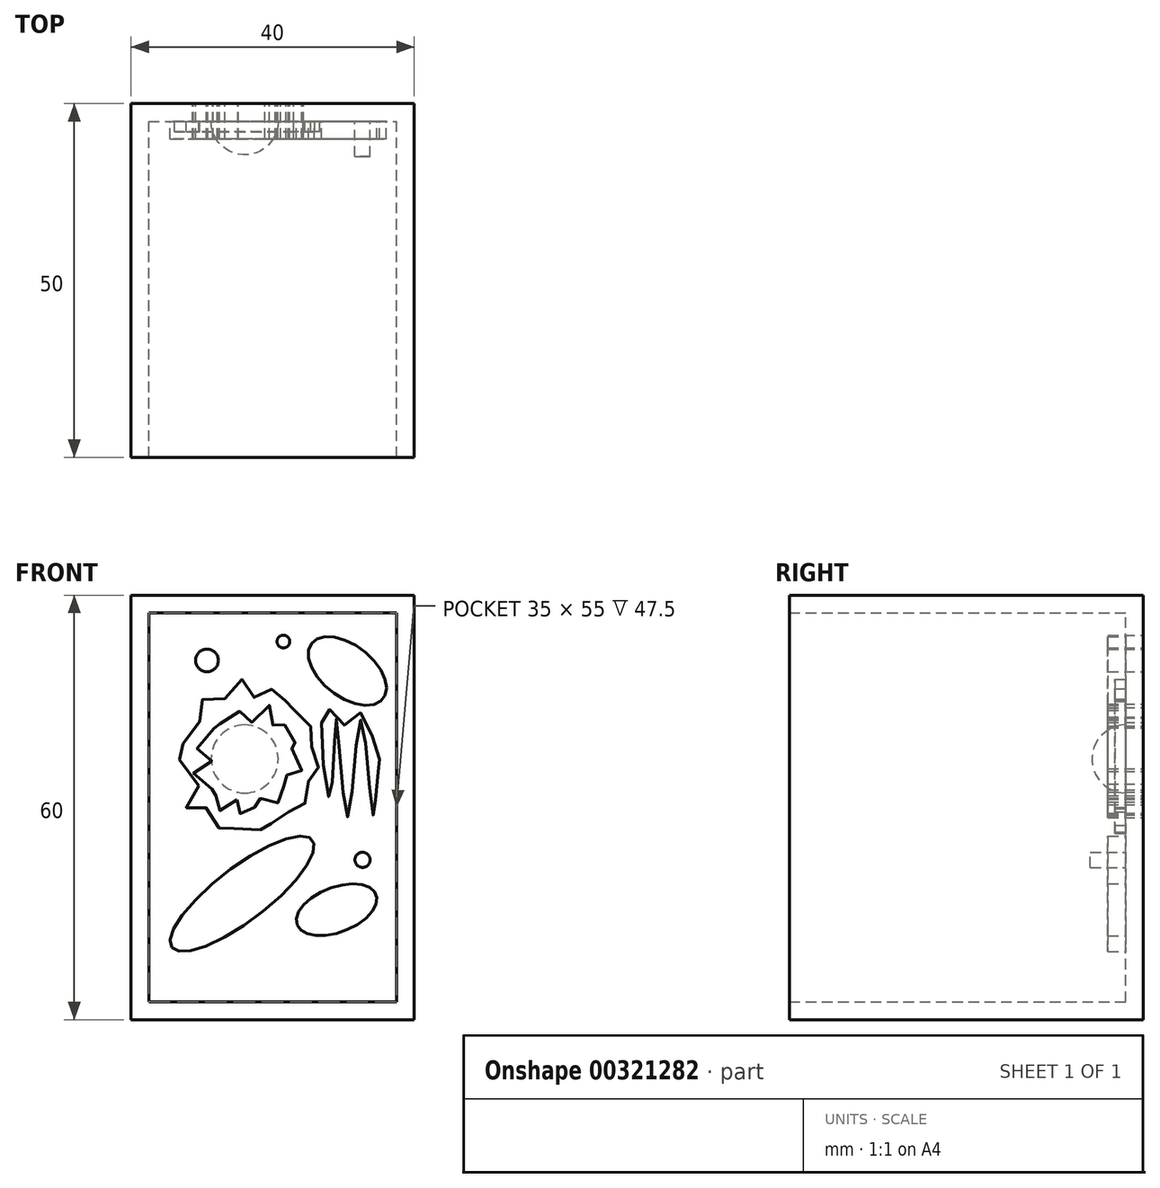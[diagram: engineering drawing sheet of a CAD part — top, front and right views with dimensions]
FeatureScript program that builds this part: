
annotation { "Feature Type Name" : "Feature", "Feature Type Description" : "" }
export const myFeature = defineFeature(function(context is Context, id is Id, definition is map)
    precondition{}
    {
        {
            var Q0;
            Q0=qCreatedBy(makeId("Front.planeOp"),FACE);
            var sketch = newSketch(context, id + "F0", { "sketchPlane" : qUnion([Q0])});
            skLineSegment(sketch, "E0.bottom", {"start": v(0, 0) * mm, "end": v(40, 0) * mm});
            skLineSegment(sketch, "E0.top", {"start": v(0, 60) * mm, "end": v(40, 60) * mm});
            skLineSegment(sketch, "E0.left", {"start": v(0, 0) * mm, "end": v(0, 60) * mm});
            skLineSegment(sketch, "E0.right", {"start": v(40, 0) * mm, "end": v(40, 60) * mm});
            skSolve(sketch);
        }
        {
            var Q0;
            Q0=makeQuery(id+"F0.imprint","IMPRINT",FACE,{"disambiguationData":[TD([[makeQuery(id+"F0.imprint","IMPRINT",EDGE,{"derivedFrom":sQuery(id+"F0.wireOp",EDGE,"E0.bottom")}),1.0]])]});
            extrude(context, id + "F1", {"entities" : qUnion([Q0]), "depth" : 25 * mm});
        }
        {
            var Q0;
            Q0=makeQuery(id+"F1.opExtrude","CAP_FACE",FACE,{"disambiguationData":[OSD([sQuery(id+"F0.wireOp",EDGE,"E0.bottom"),sQuery(id+"F0.wireOp",EDGE,"E0.top"),sQuery(id+"F0.wireOp",EDGE,"E0.left"),sQuery(id+"F0.wireOp",EDGE,"E0.right")])],"isStart":false});
            extrude(context, id + "F2", {"entities" : qUnion([Q0]), "operationType" : NewBodyOperationType.ADD, "depth" : 25 * mm});
        }
        {
            var Q0;
            Q0=makeQuery(id+"F2.opExtrude","CAP_FACE",FACE,{"disambiguationData":[OSD([sQuery(id+"F0.wireOp",EDGE,"E0.bottom"),sQuery(id+"F0.wireOp",EDGE,"E0.top"),sQuery(id+"F0.wireOp",EDGE,"E0.left"),sQuery(id+"F0.wireOp",EDGE,"E0.right")])],"isStart":false});
            shell(context, id + "F3", {"entities" : qUnion([Q0]), "thickness" : 2.5 * mm});
        }
        {
            var Q0;
            Q0=makeQuery(id+"F3.opShell","OFFSET_FACE",FACE,{"disambiguationData":[OSD([sQuery(id+"F0.wireOp",EDGE,"E0.bottom"),sQuery(id+"F0.wireOp",EDGE,"E0.top"),sQuery(id+"F0.wireOp",EDGE,"E0.left"),sQuery(id+"F0.wireOp",EDGE,"E0.right")])]});
            var sketch = newSketch(context, id + "F4", { "sketchPlane" : qUnion([Q0])});
            skLineSegment(sketch, "E1", {"start": v(16.06, 41.67) * mm, "end": v(16.06, 32.03) * mm});
            skArc(sketch, "E2", {"start": v(16.06, 32.03) * mm, "mid": v(20.8, 36.85) * mm, "end": v(16.06, 41.67) * mm});
            skSolve(sketch);
        }
        {
            var Q0;
            Q0=makeQuery(id+"F4.imprint","IMPRINT",FACE,{"disambiguationData":[TD([[makeQuery(id+"F4.imprint","IMPRINT",EDGE,{"derivedFrom":sQuery(id+"F4.wireOp",EDGE,"E1")}),1.0]])]});
            var Q1;
            Q1=sQuery(id+"F4.wireOp",EDGE,"E1");
            revolve(context, id + "F5", {"entities" : qUnion([Q0]), "axis" : qUnion([Q1]), "revolveType" : RevolveType.TWO_DIRECTIONS, "oppositeDirection" : true, "angle" : 0 * degree, "angleBack" : 180 * degree});
        }
        {
            var Q0;
            Q0=makeQuery(id+"F3.opShell","OFFSET_FACE",FACE,{"disambiguationData":[OSD([sQuery(id+"F0.wireOp",EDGE,"E0.bottom"),sQuery(id+"F0.wireOp",EDGE,"E0.top"),sQuery(id+"F0.wireOp",EDGE,"E0.left"),sQuery(id+"F0.wireOp",EDGE,"E0.right")])]});
            var sketch = newSketch(context, id + "F6", { "sketchPlane" : qUnion([Q0])});
            skEllipse(sketch, "E3", {"center": v(30.57, 49.3) * mm, "majorRadius": 6.38 * mm, "minorRadius": 3.66 * mm, "majorAxis": v(-0.8, 0.61)});
            skSolve(sketch);
        }
        {
            var Q0;
            Q0 = qSketchRegion(id + "F6", true);
            extrude(context, id + "F7", {"entities" : qUnion([Q0]), "depth" : 2.5 * mm});
        }
        {
            var Q0;
            Q0=makeQuery(id+"F3.opShell","OFFSET_FACE",FACE,{"disambiguationData":[OSD([sQuery(id+"F0.wireOp",EDGE,"E0.bottom"),sQuery(id+"F0.wireOp",EDGE,"E0.top"),sQuery(id+"F0.wireOp",EDGE,"E0.left"),sQuery(id+"F0.wireOp",EDGE,"E0.right")])]});
            var sketch = newSketch(context, id + "F8", { "sketchPlane" : qUnion([Q0])});
            skEllipse(sketch, "E4", {"center": v(29.03, 15.53) * mm, "majorRadius": 5.96 * mm, "minorRadius": 3.18 * mm, "majorAxis": v(-0.93, -0.36)});
            skSolve(sketch);
        }
        {
            var Q0;
            Q0 = qSketchRegion(id + "F8", true);
            extrude(context, id + "F9", {"entities" : qUnion([Q0]), "depth" : 2.5 * mm});
        }
        {
            var Q0;
            Q0=makeQuery(id+"F3.opShell","OFFSET_FACE",FACE,{"disambiguationData":[OSD([sQuery(id+"F0.wireOp",EDGE,"E0.bottom"),sQuery(id+"F0.wireOp",EDGE,"E0.top"),sQuery(id+"F0.wireOp",EDGE,"E0.left"),sQuery(id+"F0.wireOp",EDGE,"E0.right")])]});
            var sketch = newSketch(context, id + "F10", { "sketchPlane" : qUnion([Q0])});
            skEllipse(sketch, "E5", {"center": v(15.7, 17.8) * mm, "majorRadius": 12.5 * mm, "minorRadius": 3.77 * mm, "majorAxis": v(-0.8, -0.6)});
            skSolve(sketch);
        }
        {
            var Q0;
            Q0=makeQuery(id+"F10.imprint","IMPRINT",FACE,{"disambiguationData":[TD([[makeQuery(id+"F10.imprint","IMPRINT",EDGE,{"derivedFrom":sQuery(id+"F10.wireOp",EDGE,"E5")}),1.0]])]});
            var Q1;
            Q1=sQuery(id+"F10.wireOp",EDGE,"E5");
            extrude(context, id + "F11", {"entities" : qUnion([Q0]), "surfaceEntities" : qUnion([Q1]), "depth" : 2.5 * mm});
        }
        {
            var Q0;
            Q0=makeQuery(id+"F3.opShell","OFFSET_FACE",FACE,{"disambiguationData":[OSD([sQuery(id+"F0.wireOp",EDGE,"E0.bottom"),sQuery(id+"F0.wireOp",EDGE,"E0.top"),sQuery(id+"F0.wireOp",EDGE,"E0.left"),sQuery(id+"F0.wireOp",EDGE,"E0.right")])]});
            var sketch = newSketch(context, id + "F12", { "sketchPlane" : qUnion([Q0])});
            skFitSpline(sketch, "E6", {"points": [v(34.88, 35.03) * mm, v(34.2, 28.89) * mm, v(32.46, 42.33) * mm, v(30.58, 28.68) * mm, v(28.98, 42.47) * mm, v(28.08, 31.33) * mm, v(27.48, 43.97) * mm, v(30.64, 41.37) * mm, v(31.89, 43.69) * mm, v(35, 37.3) * mm, v(34.88, 35.03) * mm]});
            skSolve(sketch);
        }
        {
            var Q0;
            Q0=makeQuery(id+"F12.imprint","IMPRINT",FACE,{"disambiguationData":[TD([[makeQuery(id+"F12.imprint","IMPRINT",EDGE,{"derivedFrom":sQuery(id+"F12.wireOp",EDGE,"E6")}),-1.0]])]});
            extrude(context, id + "F13", {"entities" : qUnion([Q0]), "depth" : 2.5 * mm});
        }
        {
            var Q0;
            Q0=qCreatedBy(makeId("Front.planeOp"),FACE);
            var sketch = newSketch(context, id + "F14", { "sketchPlane" : qUnion([Q0])});
            skCircle(sketch, "E7", {"center": v(21.52, 53.46) * mm, "radius": 0.9 * mm});
            skSolve(sketch);
        }
        {
            var Q0;
            Q0 = qSketchRegion(id + "F14", true);
            var Q1;
            Q1=sQuery(id+"F14.wireOp",EDGE,"E7");
            extrude(context, id + "F15", {"entities" : qUnion([Q0]), "surfaceEntities" : qUnion([Q1]), "depth" : 5 * mm});
        }
        {
            var Q0;
            Q0=qCreatedBy(makeId("Front.planeOp"),FACE);
            var sketch = newSketch(context, id + "F16", { "sketchPlane" : qUnion([Q0])});
            skFitSpline(sketch, "E8", {"points": [v(14.97, 31.11) * mm, v(15.1, 28.55) * mm, v(16.75, 31.34) * mm, v(17.77, 28.9) * mm, v(18.6, 31.66) * mm, v(20.7, 30.43) * mm, v(20.49, 33.24) * mm, v(22.92, 32.5) * mm, v(21.97, 35.35) * mm, v(24.1, 35.13) * mm, v(22.22, 37.73) * mm, v(24.33, 38.85) * mm, v(23.81, 39.04) * mm, v(21.1, 40.38) * mm, v(22.35, 42.64) * mm, v(19.04, 41.58) * mm, v(19.55, 44.6) * mm, v(17.08, 42.02) * mm, v(15.45, 44.12) * mm, v(14.59, 41.33) * mm, v(10.85, 42.74) * mm, v(12.1, 39.52) * mm, v(8.71, 38.05) * mm, v(11.6, 36.25) * mm, v(8.84, 34.9) * mm, v(11.44, 33.57) * mm, v(10.66, 30.77) * mm, v(13.15, 32.14) * mm, v(12.54, 29.2) * mm, v(14.97, 31.11) * mm]});
            skSolve(sketch);
        }
        {
            var Q0;
            Q0 = qSketchRegion(id + "F16", true);
            extrude(context, id + "F17", {"entities" : qUnion([Q0]), "depth" : 5 * mm});
        }
        {
            var Q0;
            Q0=qCreatedBy(makeId("Front.planeOp"),FACE);
            var sketch = newSketch(context, id + "F18", { "sketchPlane" : qUnion([Q0])});
            skCircle(sketch, "E9", {"center": v(10.74, 50.78) * mm, "radius": 1.6 * mm});
            skSolve(sketch);
        }
        {
            var Q0;
            Q0=makeQuery(id+"F12.imprint","IMPRINT",FACE,{"disambiguationData":[TD([[makeQuery(id+"F12.imprint","IMPRINT",EDGE,{"derivedFrom":sQuery(id+"F12.wireOp",EDGE,"E6")}),1.0]])]});
            var sketch = newSketch(context, id + "F19", { "sketchPlane" : qUnion([Q0])});
            skFitSpline(sketch, "E10", {"points": [v(9.6, 33.04) * mm, v(7.8, 29.85) * mm, v(11.33, 29.73) * mm, v(12.78, 26.4) * mm, v(16.06, 27.5) * mm, v(19.5, 26.56) * mm, v(20.35, 29.03) * mm, v(24.4, 29.63) * mm, v(24.45, 33.02) * mm, v(26.62, 34.94) * mm, v(25.4, 37.8) * mm, v(25.93, 40.54) * mm, v(23, 43.76) * mm, v(23, 44.07) * mm, v(21.85, 45.08) * mm, v(20.14, 46.8) * mm, v(17.63, 45.37) * mm, v(15.76, 48.1) * mm, v(12.86, 45.14) * mm, v(9.9, 45.16) * mm, v(9.3, 40.54) * mm, v(6.12, 37.9) * mm, v(9.6, 33.04) * mm]});
            skFitSpline(sketch, "E11.0", {"points": [v(14.97, 31.11) * mm, v(15.46, 30.9) * mm, v(14.44, 25.98) * mm, v(16.95, 33.94) * mm, v(17.94, 26.46) * mm, v(17.88, 33.7) * mm, v(21.82, 28.5) * mm, v(19.1, 35) * mm, v(24.6, 30.82) * mm, v(20.28, 36.66) * mm, v(26.03, 34.05) * mm, v(20.26, 38.2) * mm, v(24.93, 38.82) * mm, v(23.65, 39.09) * mm, v(19.5, 39.74) * mm, v(24.26, 44.16) * mm, v(17.3, 39.47) * mm, v(20.8, 47.16) * mm, v(16.88, 39.65) * mm, v(15.04, 46.32) * mm, v(15.72, 39.05) * mm, v(8.67, 44.8) * mm, v(14.5, 38.44) * mm, v(5.8, 38.46) * mm, v(14.35, 36.14) * mm, v(6.39, 34.73) * mm, v(13.3, 34.43) * mm, v(9, 29) * mm, v(14.71, 34.22) * mm, v(11.1, 26.81) * mm, v(14.44, 31.35) * mm, v(14.97, 31.11) * mm]});
            skFitSpline(sketch, "E12.0", {"points": [v(14.97, 31.11) * mm, v(15.46, 30.9) * mm, v(14.44, 25.98) * mm, v(16.95, 33.94) * mm, v(17.94, 26.46) * mm, v(17.88, 33.7) * mm, v(21.82, 28.5) * mm, v(19.1, 35) * mm, v(24.6, 30.82) * mm, v(20.28, 36.66) * mm, v(26.03, 34.05) * mm, v(20.26, 38.2) * mm, v(24.93, 38.82) * mm, v(23.65, 39.09) * mm, v(19.5, 39.74) * mm, v(24.26, 44.16) * mm, v(17.3, 39.47) * mm, v(20.8, 47.16) * mm, v(16.88, 39.65) * mm, v(15.04, 46.32) * mm, v(15.72, 39.05) * mm, v(8.67, 44.8) * mm, v(14.5, 38.44) * mm, v(5.8, 38.46) * mm, v(14.35, 36.14) * mm, v(6.39, 34.73) * mm, v(13.3, 34.43) * mm, v(9, 29) * mm, v(14.71, 34.22) * mm, v(11.1, 26.81) * mm, v(14.44, 31.35) * mm, v(14.97, 31.11) * mm]});
            skSolve(sketch);
        }
        {
            var Q0;
            Q0=makeQuery(id+"F19.imprint","IMPRINT",FACE,{"disambiguationData":[TD([[makeQuery(id+"F19.imprint","IMPRINT",EDGE,{"derivedFrom":sQuery(id+"F19.wireOp",EDGE,"E10")}),1.0]])]});
            extrude(context, id + "F20", {"entities" : qUnion([Q0]), "depth" : 1.5 * mm});
        }
        {
            var Q0;
            Q0=makeQuery(id+"F18.imprint","IMPRINT",FACE,{"disambiguationData":[TD([[makeQuery(id+"F18.imprint","IMPRINT",EDGE,{"derivedFrom":sQuery(id+"F18.wireOp",EDGE,"E9")}),1.0]])]});
            var Q1;
            Q1=sQuery(id+"F18.wireOp",EDGE,"E9");
            extrude(context, id + "F21", {"entities" : qUnion([Q0]), "surfaceEntities" : qUnion([Q1]), "depth" : 5 * mm});
        }
        {
            var Q0;
            Q0=makeQuery(id+"F3.opShell","OFFSET_FACE",FACE,{"disambiguationData":[OSD([sQuery(id+"F0.wireOp",EDGE,"E0.bottom"),sQuery(id+"F0.wireOp",EDGE,"E0.top"),sQuery(id+"F0.wireOp",EDGE,"E0.left"),sQuery(id+"F0.wireOp",EDGE,"E0.right")])]});
            var sketch = newSketch(context, id + "F22", { "sketchPlane" : qUnion([Q0])});
            skCircle(sketch, "E13", {"center": v(32.7, 22.59) * mm, "radius": 1.07 * mm});
            skSolve(sketch);
        }
        {
            var Q0;
            Q0=makeQuery(id+"F22.imprint","IMPRINT",FACE,{"disambiguationData":[TD([[makeQuery(id+"F22.imprint","IMPRINT",EDGE,{"derivedFrom":sQuery(id+"F22.wireOp",EDGE,"E13")}),1.0]])]});
            extrude(context, id + "F23", {"entities" : qUnion([Q0]), "depth" : 5 * mm});
        }
    });
